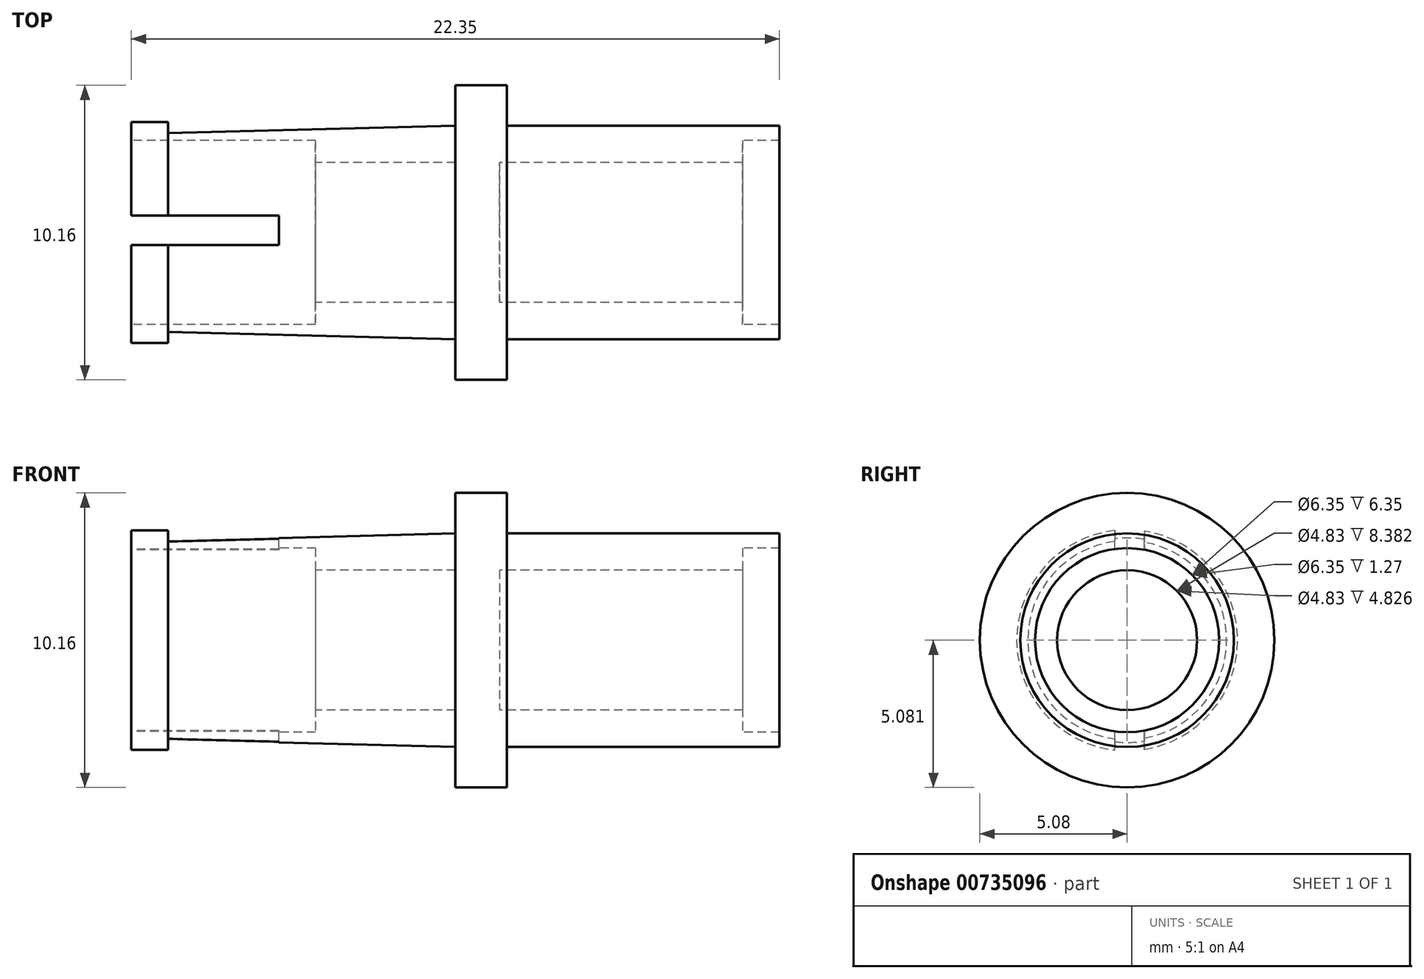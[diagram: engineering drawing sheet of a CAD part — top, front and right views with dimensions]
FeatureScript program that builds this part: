
annotation { "Feature Type Name" : "Feature", "Feature Type Description" : "" }
export const myFeature = defineFeature(function(context is Context, id is Id, definition is map)
    precondition{}
    {
        {
            var Q0;
            Q0=qCreatedBy(makeId("Front.planeOp"),FACE);
            var sketch = newSketch(context, id + "F0", { "sketchPlane" : qUnion([Q0])});
            skLineSegment(sketch, "E0", {"start": v(-10.17, -9.6) * mm, "end": v(-8.65, -9.6) * mm});
            skLineSegment(sketch, "E1", {"start": v(-8.65, -9.6) * mm, "end": v(-8.65, -7.2) * mm});
            skLineSegment(sketch, "E2", {"start": v(-8.65, -7.2) * mm, "end": v(-0.27, -7.2) * mm});
            skLineSegment(sketch, "E3", {"start": v(-0.27, -7.2) * mm, "end": v(-0.27, -6.43) * mm});
            skLineSegment(sketch, "E4", {"start": v(-0.27, -6.43) * mm, "end": v(1, -6.43) * mm});
            skLineSegment(sketch, "E5", {"start": v(1, -6.43) * mm, "end": v(1, -5.93) * mm});
            skLineSegment(sketch, "E6", {"start": v(1, -5.93) * mm, "end": v(-8.4, -5.93) * mm});
            skLineSegment(sketch, "E7", {"start": v(-8.4, -5.93) * mm, "end": v(-8.4, -4.53) * mm});
            skLineSegment(sketch, "E8", {"start": v(-8.4, -4.53) * mm, "end": v(-10.17, -4.53) * mm});
            skLineSegment(sketch, "E9", {"start": v(-10.17, -4.53) * mm, "end": v(-10.17, -5.93) * mm});
            skLineSegment(sketch, "E10", {"start": v(-10.17, -5.93) * mm, "end": v(-20.08, -6.18) * mm});
            skLineSegment(sketch, "E11", {"start": v(-20.08, -6.18) * mm, "end": v(-20.08, -5.8) * mm});
            skLineSegment(sketch, "E12", {"start": v(-20.08, -5.8) * mm, "end": v(-21.35, -5.8) * mm});
            skLineSegment(sketch, "E13", {"start": v(-21.35, -5.8) * mm, "end": v(-21.35, -6.43) * mm});
            skLineSegment(sketch, "E14", {"start": v(-21.35, -6.43) * mm, "end": v(-15, -6.43) * mm});
            skLineSegment(sketch, "E15", {"start": v(-15, -6.43) * mm, "end": v(-15, -7.2) * mm});
            skLineSegment(sketch, "E16", {"start": v(-15, -7.2) * mm, "end": v(-10.17, -7.2) * mm});
            skLineSegment(sketch, "E17", {"start": v(-10.17, -7.2) * mm, "end": v(-10.17, -9.6) * mm});
            skLineSegment(sketch, "E18", {"start": v(-16.9, -9.6) * mm, "end": v(5.35, -9.6) * mm, "construction": true});
            skLineSegment(sketch, "E19.MirrorCS", {"start": v(1, -12.78) * mm, "end": v(1, -13.3) * mm});
            skLineSegment(sketch, "E20.MirrorCS", {"start": v(-20.08, -13.04) * mm, "end": v(-20.08, -13.42) * mm});
            skLineSegment(sketch, "E21.MirrorCS", {"start": v(-0.27, -12.02) * mm, "end": v(-0.27, -12.78) * mm});
            skLineSegment(sketch, "E22.MirrorCS", {"start": v(-15, -12.02) * mm, "end": v(-10.17, -12.02) * mm});
            skLineSegment(sketch, "E23.MirrorCS", {"start": v(-10.17, -13.3) * mm, "end": v(-20.08, -13.04) * mm});
            skLineSegment(sketch, "E24.MirrorCS", {"start": v(-8.4, -13.3) * mm, "end": v(-8.4, -14.69) * mm});
            skLineSegment(sketch, "E25.MirrorCS", {"start": v(-15, -12.78) * mm, "end": v(-15, -12.02) * mm});
            skLineSegment(sketch, "E26.MirrorCS", {"start": v(-8.65, -9.6) * mm, "end": v(-8.65, -12.02) * mm});
            skLineSegment(sketch, "E27.MirrorCS", {"start": v(1, -13.3) * mm, "end": v(-8.4, -13.3) * mm});
            skLineSegment(sketch, "E28.MirrorCS", {"start": v(-8.65, -12.02) * mm, "end": v(-0.27, -12.02) * mm});
            skLineSegment(sketch, "E29.MirrorCS", {"start": v(-0.27, -12.78) * mm, "end": v(1, -12.78) * mm});
            skLineSegment(sketch, "E30.MirrorCS", {"start": v(-10.17, -14.69) * mm, "end": v(-10.17, -13.3) * mm});
            skLineSegment(sketch, "E31.MirrorCS", {"start": v(-10.17, -12.02) * mm, "end": v(-10.17, -9.6) * mm});
            skLineSegment(sketch, "E32.MirrorCS", {"start": v(-21.35, -12.78) * mm, "end": v(-15, -12.78) * mm});
            skLineSegment(sketch, "E33.MirrorCS", {"start": v(-21.35, -13.42) * mm, "end": v(-21.35, -12.78) * mm});
            skLineSegment(sketch, "E34.MirrorCS", {"start": v(-20.08, -13.42) * mm, "end": v(-21.35, -13.42) * mm});
            skLineSegment(sketch, "E35.MirrorCS", {"start": v(-8.4, -14.69) * mm, "end": v(-10.17, -14.69) * mm});
            skSolve(sketch);
        }
        {
            var Q0;
            Q0=makeQuery(id+"F0.imprint","IMPRINT",FACE,{"disambiguationData":[TD([[makeQuery(id+"F0.imprint","IMPRINT",EDGE,{"derivedFrom":sQuery(id+"F0.wireOp",EDGE,"E1")}),1.0]])]});
            var Q1;
            Q1=sQuery(id+"F0.wireOp",EDGE,"E18");
            revolve(context, id + "F1", {"entities" : qUnion([Q0]), "axis" : qUnion([Q1]), "revolveType" : RevolveType.FULL});
        }
        {
            var Q0;
            Q0=qCreatedBy(makeId("Top.planeOp"),FACE);
            var sketch = newSketch(context, id + "F2", { "sketchPlane" : qUnion([Q0])});
            skLineSegment(sketch, "E36", {"start": v(-21.35, 0.59) * mm, "end": v(-16.27, 0.59) * mm});
            skLineSegment(sketch, "E37", {"start": v(-16.27, 0.59) * mm, "end": v(-16.27, -0.43) * mm});
            skLineSegment(sketch, "E38", {"start": v(-16.27, -0.43) * mm, "end": v(-21.35, -0.43) * mm});
            skLineSegment(sketch, "E39", {"start": v(-21.35, -0.43) * mm, "end": v(-21.35, 0.59) * mm});
            skSolve(sketch);
        }
        {
            var Q0;
            Q0=qSketchRegion(id+"F2",true);
            extrude(context, id + "F3", {"entities" : qUnion([Q0]), "operationType" : NewBodyOperationType.REMOVE, "oppositeDirection" : true, "depth" : 25.4 * mm, "offsetDistance" : 25.4 * mm});
        }
    });
